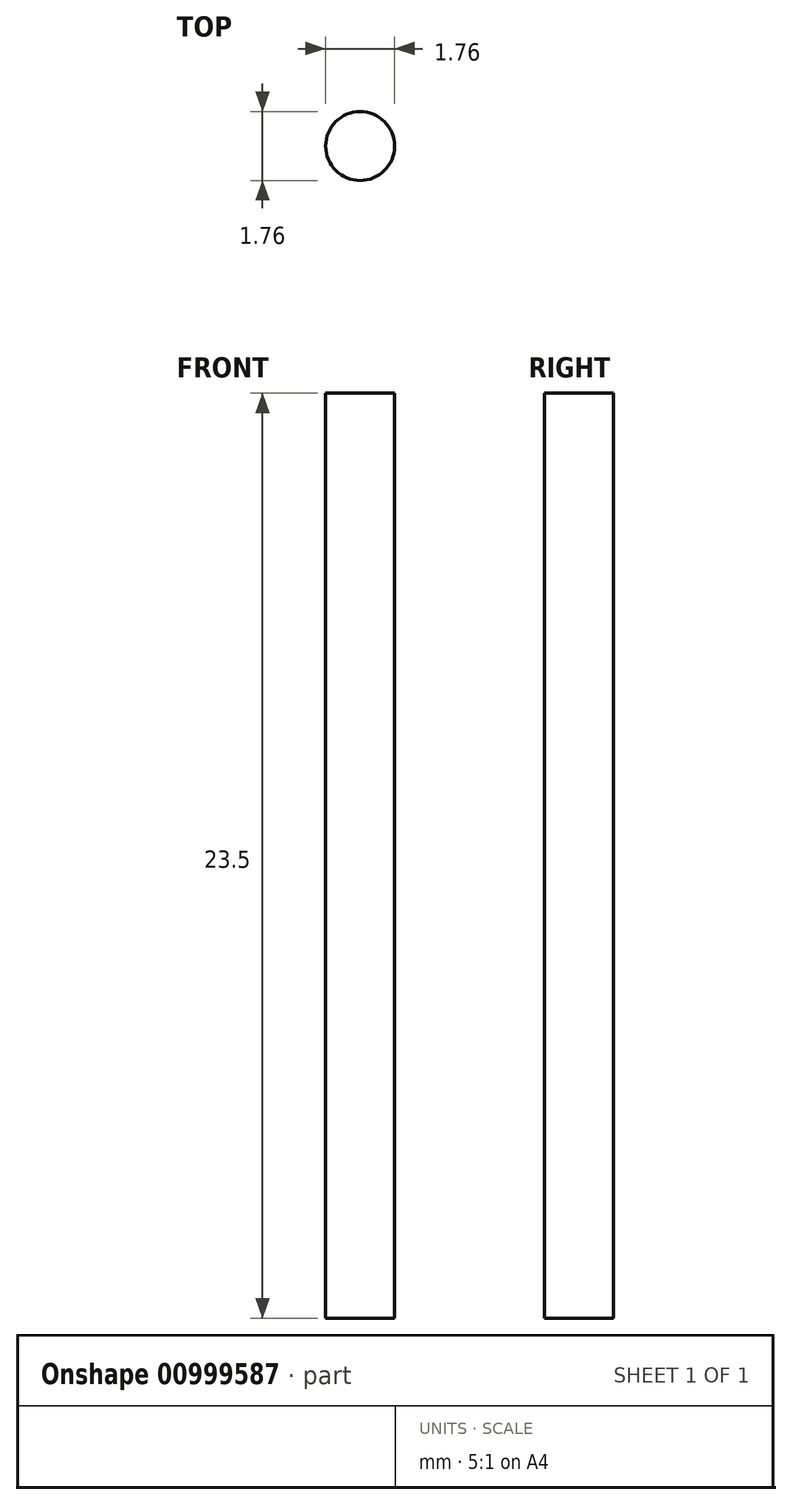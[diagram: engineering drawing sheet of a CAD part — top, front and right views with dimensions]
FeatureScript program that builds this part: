
annotation { "Feature Type Name" : "Feature", "Feature Type Description" : "" }
export const myFeature = defineFeature(function(context is Context, id is Id, definition is map)
    precondition{}
    {
        {
            var Q0;
            Q0=qCreatedBy(makeId("Top.planeOp"),FACE);
            var sketch = newSketch(context, id + "F0", { "sketchPlane" : qUnion([Q0])});
            skCircle(sketch, "E0", {"center": v(0, 0) * mm, "radius": 0.88 * mm});
            skSolve(sketch);
        }
        {
            var Q0;
            Q0 = qSketchRegion(id + "F0", true);
            extrude(context, id + "F1", {"entities" : qUnion([Q0]), "depth" : 23.5 * mm, "offsetDistance" : 25 * mm});
        }
    });
